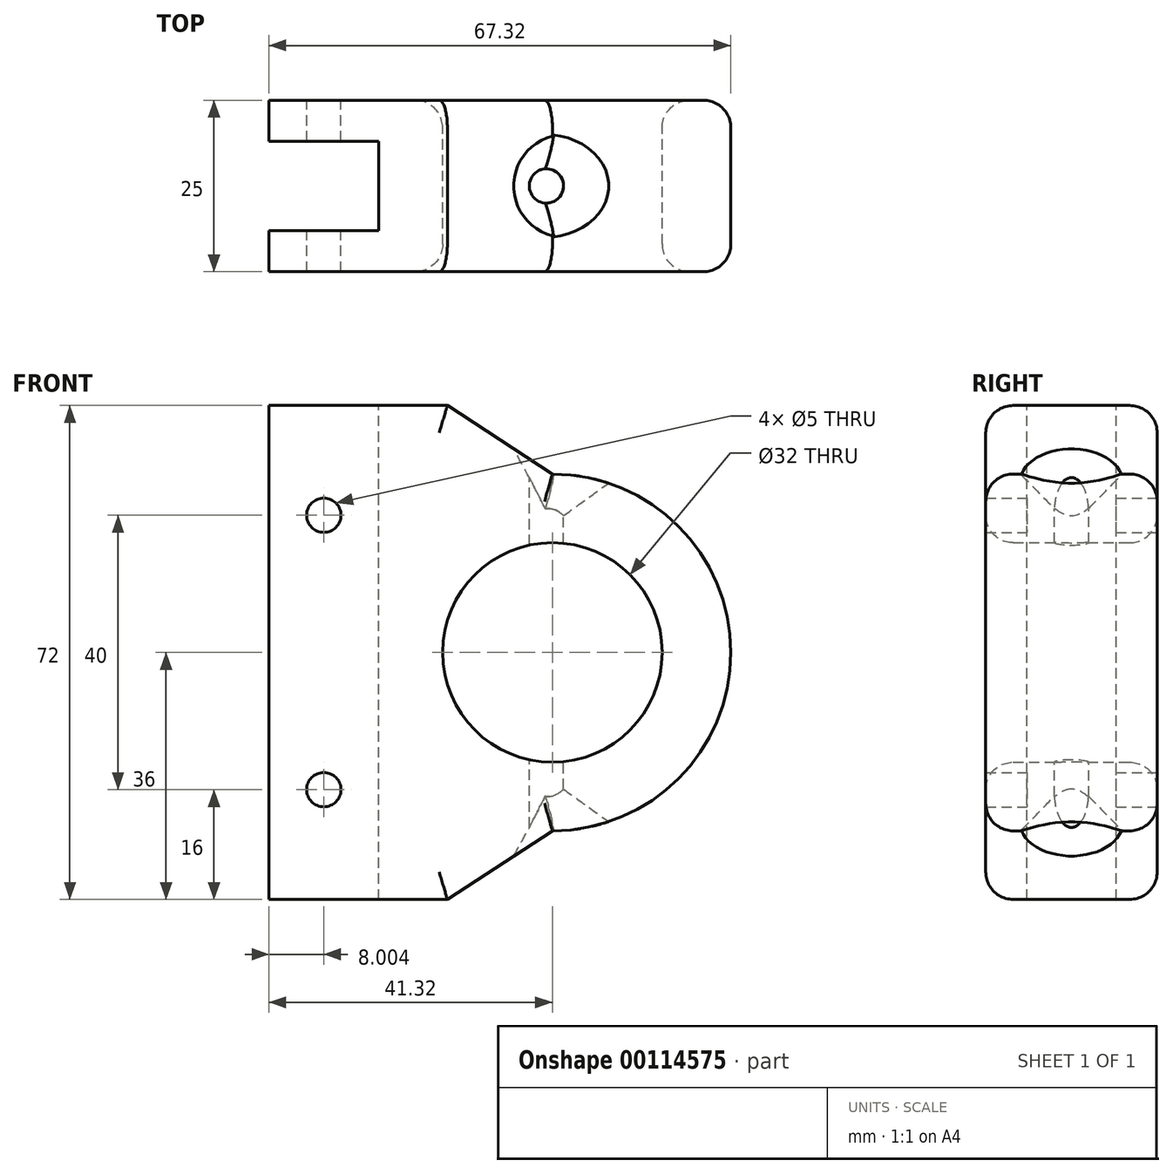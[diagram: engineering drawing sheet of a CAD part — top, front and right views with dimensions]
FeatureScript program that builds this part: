
annotation { "Feature Type Name" : "Feature", "Feature Type Description" : "" }
export const myFeature = defineFeature(function(context is Context, id is Id, definition is map)
    precondition{}
    {
        {
            assignVariable(context, id + "F0", {"name" : "BoardThickness", "anyValue" : 13});
        }
        {
            var Q0;
            Q0=qCreatedBy(makeId("Front.planeOp"),FACE);
            var sketch = newSketch(context, id + "F1", { "sketchPlane" : qUnion([Q0])});
            skCircle(sketch, "E0", {"center": v(26, 36) * mm, "radius": 16 * mm});
            skCircle(sketch, "E1.0", {"center": v(26, 36) * mm, "radius": 26 * mm, "construction": true});
            skLineSegment(sketch, "E2", {"start": v(-15.32, 0) * mm, "end": v(-15.32, 72) * mm});
            skLineSegment(sketch, "E3", {"start": v(-15.32, 72) * mm, "end": v(10.7, 72) * mm});
            skLineSegment(sketch, "E4", {"start": v(10.7, 72) * mm, "end": v(26, 62) * mm});
            skLineSegment(sketch, "E5", {"start": v(-15.32, 0) * mm, "end": v(10.7, 0) * mm});
            skLineSegment(sketch, "E6", {"start": v(10.7, 0) * mm, "end": v(26, 10) * mm});
            skArc(sketch, "E7", {"start": v(26, 10) * mm, "mid": v(52, 36) * mm, "end": v(26, 62) * mm});
            skCircle(sketch, "E8", {"center": v(-7.32, 56) * mm, "radius": 2.5 * mm});
            skCircle(sketch, "E9", {"center": v(-7.32, 16) * mm, "radius": 2.5 * mm});
            skSolve(sketch);
        }
        {
            var Q0;
            Q0=makeQuery(id+"F1.imprint","IMPRINT",FACE,{"disambiguationData":[TD([[makeQuery(id+"F1.imprint","IMPRINT",EDGE,{"derivedFrom":sQuery(id+"F1.wireOp",EDGE,"E0")}),-1.0]])]});
            extrude(context, id + "F2", {"entities" : qUnion([Q0]), "depth" : (getVariable(context, 'BoardThickness') + 12) * mm});
        }
        {
            var Q0;
            Q0=makeQuery(id+"F2.opExtrude","SWEPT_FACE",FACE,{"disambiguationData":[OSD([sQuery(id+"F1.wireOp",EDGE,"E3")])]});
            var sketch = newSketch(context, id + "F3", { "sketchPlane" : qUnion([Q0])});
            skLineSegment(sketch, "E10", {"start": v(-15.32, -6) * mm, "end": v(0.68, -6) * mm});
            skLineSegment(sketch, "E11", {"start": v(0.68, -6) * mm, "end": v(0.68, -19) * mm});
            skLineSegment(sketch, "E12", {"start": v(0.68, -19) * mm, "end": v(-15.32, -19) * mm});
            skCircle(sketch, "E13", {"center": v(25.13, -12.5) * mm, "radius": 2.5 * mm});
            skLineSegment(sketch, "E14", {"start": v(17.13, 0) * mm, "end": v(17.13, -25) * mm, "construction": true});
            skLineSegment(sketch, "E15", {"start": v(17.13, -12.5) * mm, "end": v(25.13, -12.5) * mm, "construction": true});
            skSolve(sketch);
        }
        {
            var Q0;
            {var subQ0=sQuery(id+"F3.wireOp",EDGE,"E10");Q0=makeQuery(id+"F3.imprint","IMPRINT",FACE,{"disambiguationData":[TD([[makeQuery(id+"F3.imprint","IMPRINT",EDGE,{"derivedFrom":subQ0}),-1.0]])]});}
            var Q1;
            Q1=makeQuery(id+"F3.imprint","IMPRINT",FACE,{"disambiguationData":[TD([[makeQuery(id+"F3.imprint","IMPRINT",EDGE,{"derivedFrom":sQuery(id+"F3.wireOp",EDGE,"E13")}),1.0]])]});
            var Q2;
            Q2=makeQuery(id+"F2.opExtrude","SWEPT_FACE",FACE,{"disambiguationData":[OSD([sQuery(id+"F1.wireOp",EDGE,"E5")])]});
            extrude(context, id + "F4", {"entities" : qUnion([Q0, Q1]), "operationType" : NewBodyOperationType.REMOVE, "endBound" : BoundingType.UP_TO_SURFACE, "oppositeDirection" : true, "endBoundEntityFace" : qUnion([Q2]), "depth" : 19.52 * mm});
        }
        {
            var Q0;
            Q0=makeQuery(id+"F2.opExtrude","CAP_EDGE",EDGE,{"disambiguationData":[OSD([sQuery(id+"F1.wireOp",EDGE,"E0")])],"isStart":false});
            var Q1;
            Q1=makeQuery(id+"F2.opExtrude","CAP_EDGE",EDGE,{"disambiguationData":[OSD([sQuery(id+"F1.wireOp",EDGE,"E0")])],"isStart":true});
            var Q2;
            Q2=makeQuery(id+"F2.opExtrude","CAP_EDGE",EDGE,{"disambiguationData":[OSD([sQuery(id+"F1.wireOp",EDGE,"E7")])],"isStart":false});
            var Q3;
            Q3=makeQuery(id+"F2.opExtrude","CAP_EDGE",EDGE,{"disambiguationData":[OSD([sQuery(id+"F1.wireOp",EDGE,"E7")])],"isStart":true});
            var Q4;
            Q4=makeQuery(id+"F2.opExtrude","CAP_EDGE",EDGE,{"disambiguationData":[OSD([sQuery(id+"F1.wireOp",EDGE,"E4")])],"isStart":false});
            var Q5;
            Q5=makeQuery(id+"F2.opExtrude","CAP_EDGE",EDGE,{"disambiguationData":[OSD([sQuery(id+"F1.wireOp",EDGE,"E4")])],"isStart":true});
            var Q6;
            Q6=makeQuery(id+"F2.opExtrude","CAP_EDGE",EDGE,{"disambiguationData":[OSD([sQuery(id+"F1.wireOp",EDGE,"E6")])],"isStart":false});
            var Q7;
            Q7=makeQuery(id+"F2.opExtrude","CAP_EDGE",EDGE,{"disambiguationData":[OSD([sQuery(id+"F1.wireOp",EDGE,"E6")])],"isStart":true});
            var Q8;
            Q8=makeQuery(id+"F2.opExtrude","CAP_EDGE",EDGE,{"disambiguationData":[OSD([sQuery(id+"F1.wireOp",EDGE,"E3")])],"isStart":false});
            var Q9;
            Q9=makeQuery(id+"F2.opExtrude","CAP_EDGE",EDGE,{"disambiguationData":[OSD([sQuery(id+"F1.wireOp",EDGE,"E3")])],"isStart":true});
            var Q10;
            Q10=makeQuery(id+"F2.opExtrude","CAP_EDGE",EDGE,{"disambiguationData":[OSD([sQuery(id+"F1.wireOp",EDGE,"E5")])],"isStart":false});
            var Q11;
            Q11=makeQuery(id+"F2.opExtrude","CAP_EDGE",EDGE,{"disambiguationData":[OSD([sQuery(id+"F1.wireOp",EDGE,"E5")])],"isStart":true});
            fillet(context, id + "F5", {"entities" : qUnion([Q0, Q1, Q2, Q3, Q4, Q5, Q6, Q7, Q8, Q9, Q10, Q11]), "radius" : 4 * mm, "tangentPropagation" : true, "allowEdgeOverflow" : false});
        }
        {
            var Q0;
            Q0=makeQuery(id+"F4.boolean.opBoolean","INTERSECT",EDGE,{"derivedFrom":[makeQuery(id+"F2.opExtrude","SWEPT_FACE",FACE,{"disambiguationData":[OSD([sQuery(id+"F1.wireOp",EDGE,"E6")])]}),makeQuery(id+"F4.opExtrude","SWEPT_FACE",FACE,{"disambiguationData":[OSD([sQuery(id+"F3.wireOp",EDGE,"E13")])]})]});
            var Q1;
            Q1=makeQuery(id+"F4.boolean.opBoolean","INTERSECT",EDGE,{"disambiguationData":[OD(1.0)],"derivedFrom":[makeQuery(id+"F2.opExtrude","SWEPT_FACE",FACE,{"disambiguationData":[OSD([sQuery(id+"F1.wireOp",EDGE,"E7")])]}),makeQuery(id+"F4.opExtrude","SWEPT_FACE",FACE,{"disambiguationData":[OSD([sQuery(id+"F3.wireOp",EDGE,"E13")])]})]});
            var Q2;
            Q2=makeQuery(id+"F4.boolean.opBoolean","INTERSECT",EDGE,{"derivedFrom":[makeQuery(id+"F2.opExtrude","SWEPT_FACE",FACE,{"disambiguationData":[OSD([sQuery(id+"F1.wireOp",EDGE,"E4")])]}),makeQuery(id+"F4.opExtrude","SWEPT_FACE",FACE,{"disambiguationData":[OSD([sQuery(id+"F3.wireOp",EDGE,"E13")])]})]});
            var Q3;
            Q3=makeQuery(id+"F4.boolean.opBoolean","INTERSECT",EDGE,{"disambiguationData":[OD(0.0)],"derivedFrom":[makeQuery(id+"F2.opExtrude","SWEPT_FACE",FACE,{"disambiguationData":[OSD([sQuery(id+"F1.wireOp",EDGE,"E7")])]}),makeQuery(id+"F4.opExtrude","SWEPT_FACE",FACE,{"disambiguationData":[OSD([sQuery(id+"F3.wireOp",EDGE,"E13")])]})]});
            chamfer(context, id + "F6", {"entities" : qUnion([Q0, Q1, Q2, Q3]), "width" : 5 * mm, "tangentPropagation" : true});
        }
    });
